FCSTD DOCUMENT  (FreeCAD 0.19R0.19.2)
Label: 002
License: All rights reserved
LicenseURL: http://en.wikipedia.org/wiki/All_rights_reserved
objects: Sketcher::SketchObject×1
note: 1 computed .brp shape members not serialized (recipe doc carries the construction recipe); baked Part::Feature solids carry a one-line shape summary decoded from their .brp

FEATURE [Sketcher::SketchObject] Sketch
  FullyConstrained = false
  sketch-geometry (8):
    g0: LineSegment StartX=0 StartY=0 StartZ=0 EndX=10.2 EndY=0 EndZ=0
    g1: LineSegment StartX=0 StartY=0 StartZ=0 EndX=0 EndY=7.8 EndZ=0
    g2: LineSegment StartX=0 StartY=0 StartZ=0 EndX=0 EndY=-7.8 EndZ=0
    g3: Circle CenterX=0 CenterY=0 CenterZ=0 NormalX=0 NormalY=0 NormalZ=1 AngleXU=0 Radius=10.2
    g4: LineSegment StartX=0 StartY=7.8 StartZ=0 EndX=10.2367 EndY=7.8 EndZ=0
    g5: LineSegment StartX=0 StartY=7.8 StartZ=0 EndX=-9.08332 EndY=7.8 EndZ=0
    g6: LineSegment StartX=0 StartY=-7.8 StartZ=0 EndX=-8.66818 EndY=-7.8 EndZ=0
    g7: LineSegment StartX=0 StartY=-7.8 StartZ=0 EndX=8.64004 EndY=-7.8 EndZ=0
  constraints (20):
    c: Horizontal(g0)
    c: Distance(g0) = 10.2
    c: Coincident(g0,g-1)
    c: Vertical(g1)
    c: Distance(g1) = 7.8
    c: Coincident(g1,g0)
    c: Vertical(g2)
    c: Distance(g2) = 7.8
    c: Coincident(g2,g0)
    c: Coincident(g3,g0)
    c: PointOnObject(g0,g3)
    c: Coincident(g4,g1)
    c: Horizontal(g4)
    c: Coincident(g5,g1)
    c: Horizontal(g5)
    c: Coincident(g6,g2)
    c: Horizontal(g6)
    c: Coincident(g7,g2)
    c: Horizontal(g7)
    c: Block(g3)
